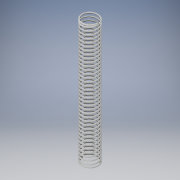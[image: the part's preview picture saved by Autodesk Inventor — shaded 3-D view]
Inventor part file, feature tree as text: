
AUTODESK INVENTOR PART (.ipt)
format: ipt  version: 2018 (Build 220112000, 112)  size: 839,680 bytes
history: native  units: in
note: dims shown in document units (in); Inventor stores cm internally (conversion verified against a paired STEP export)
features: helix x1, sketch x1
ambient origin geometry x8: Origin, YZ Plane, XZ Plane, XY Plane, X Axis, Y Axis, Z Axis, Center Point
bodies: Solid1 (feature_tree)
feature tree (2):
  helix  "Coil1"  [1 undecoded]
  sketch  "Sketch1"  dims[d1=0.47in d2=1.0in d3=6.9026in d4=14.1732in d5=0.0in d6=90.0deg d7=180.0deg d8=90.0deg d9=180.0deg]
note: 1 required parameter value undecoded (feature->parameter linkage not recoverable at this tier; creation-order binding heuristic only, values carry confidence <= 0.55)
